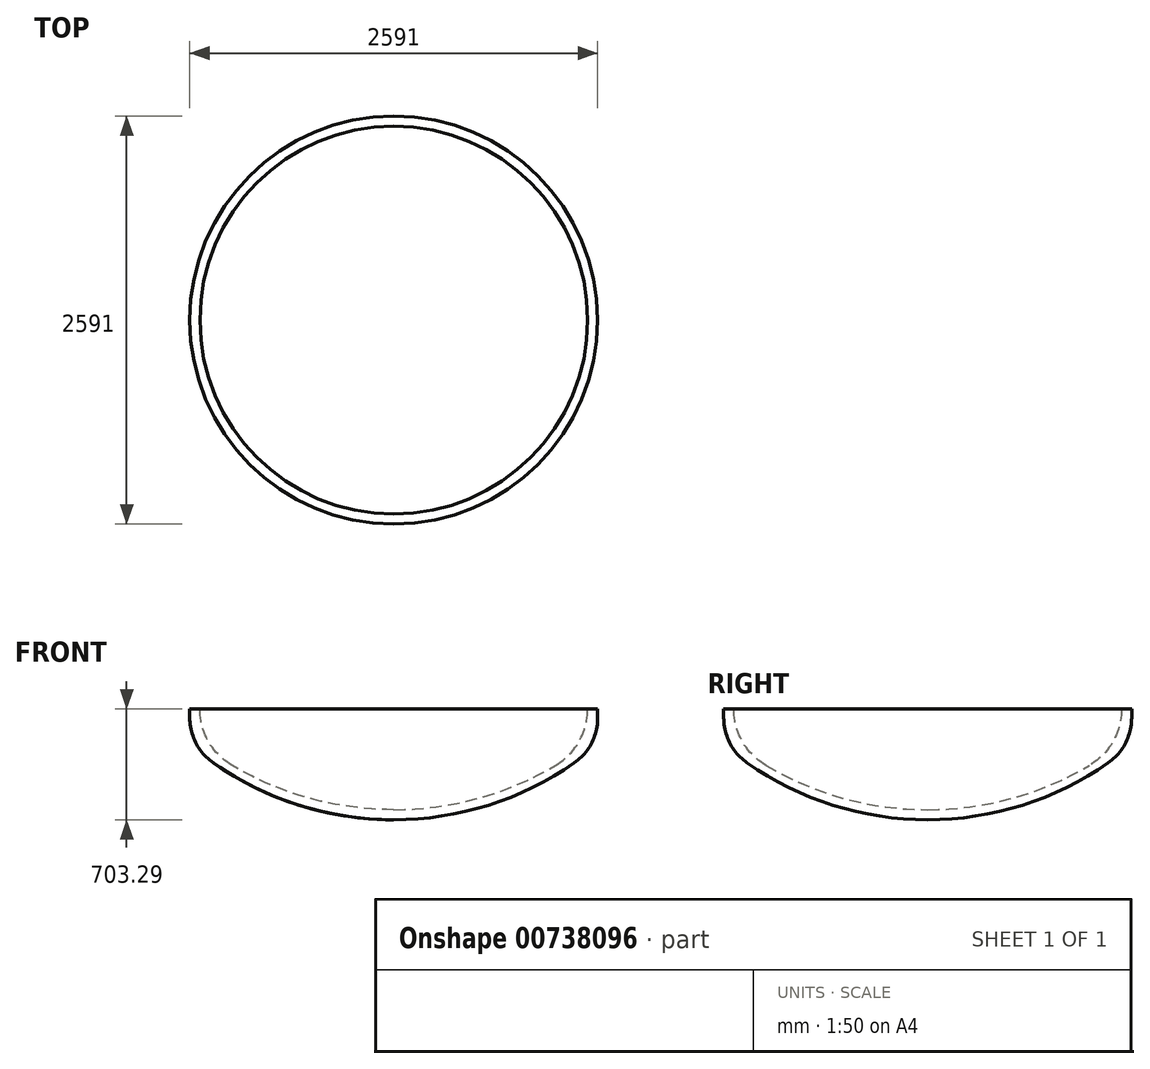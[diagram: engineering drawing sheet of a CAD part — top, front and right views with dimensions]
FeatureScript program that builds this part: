
annotation { "Feature Type Name" : "Feature", "Feature Type Description" : "" }
export const myFeature = defineFeature(function(context is Context, id is Id, definition is map)
    precondition{}
    {
        {
            var Q0;
            Q0=qCreatedBy(makeId("Front.planeOp"),FACE);
            var sketch = newSketch(context, id + "F0", { "sketchPlane" : qUnion([Q0])});
            skArc(sketch, "E0", {"start": v(-1027.88, -357.75) * mm, "mid": v(-532.9, -567.78) * mm, "end": v(0, -639.5) * mm});
            skArc(sketch, "E1", {"start": v(-1231.7, 0) * mm, "mid": v(-1177.17, -205.87) * mm, "end": v(-1027.88, -357.75) * mm});
            skPoint(sketch, "E2.center.orphan", {"position": v(0, 0) * mm});
            skPoint(sketch, "E2.end.orphan", {"position": v(966.7, -402.57) * mm});
            skLineSegment(sketch, "E3", {"start": v(0, -639.5) * mm, "end": v(0, -703.3) * mm});
            skArc(sketch, "E4", {"start": v(-1146.06, -342.36) * mm, "mid": v(-600.78, -610.93) * mm, "end": v(0, -703.3) * mm});
            skArc(sketch, "E5", {"start": v(-1295.5, -55.52) * mm, "mid": v(-1255.9, -217.24) * mm, "end": v(-1146.06, -342.36) * mm});
            skLineSegment(sketch, "E6", {"start": v(-1295.5, -55.52) * mm, "end": v(-1295.5, 0) * mm});
            skLineSegment(sketch, "E7", {"start": v(-1295.5, 0) * mm, "end": v(-1231.7, 0) * mm});
            skSolve(sketch);
        }
        {
            var Q0;
            Q0=makeQuery(id+"F0.imprint","IMPRINT",FACE,{"disambiguationData":[TD([[makeQuery(id+"F0.imprint","IMPRINT",EDGE,{"derivedFrom":sQuery(id+"F0.wireOp",EDGE,"E0")}),1.0]])]});
            var Q1;
            Q1=makeQuery(id+"F0.imprint","IMPRINT",FACE,{"disambiguationData":[TD([[makeQuery(id+"F0.imprint","IMPRINT",EDGE,{"derivedFrom":sQuery(id+"F0.wireOp",EDGE,"E0")}),-1.0]])]});
            var Q2;
            Q2=sQuery(id+"F0.wireOp",EDGE,"E3");
            revolve(context, id + "F1", {"surfaceOperationType" : NewSurfaceOperationType.NEW, "entities" : qUnion([Q0, Q1]), "axis" : qUnion([Q2]), "revolveType" : RevolveType.FULL});
        }
    });
